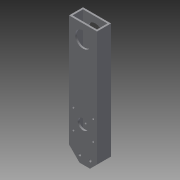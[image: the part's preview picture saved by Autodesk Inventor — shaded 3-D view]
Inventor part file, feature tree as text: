
AUTODESK INVENTOR PART (.ipt)
format: ipt  version: 2013 (Build 170138000, 138)  size: 178,176 bytes
history: native  units: in
note: dims shown in document units (in); Inventor stores cm internally (conversion verified against a paired STEP export)
features: extrude x7, sketch x7
ambient origin geometry x8: Origin, YZ Plane, XZ Plane, XY Plane, X Axis, Y Axis, Z Axis, Center Point
bodies: Solid1 (feature_tree)
feature tree (14):
  extrude  "Extrusion1"  Depth=1.0in
  extrude  "Extrusion2"  Depth=0.75in
  extrude  "Extrusion3"  Depth=1.0in
  extrude  "Extrusion4"  Depth=7.0in
  extrude  "Extrusion5"  Depth=0.25in
  extrude  "Extrusion6"  Depth=0.5in
  extrude  "Extrusion7"  TaperAngle=0.0deg  [1 undecoded]
  sketch  "Sketch1"  dims[d0=2.0in d1=1.0in]
  sketch  "Sketch2"  dims[d2=1.75in d3=0.75in]
  sketch  "Sketch3"  dims[d4=9.0in d5=0.0in d6=1.0in]
  sketch  "Sketch4"  dims[d7=0.5in d8=7.0in]
  sketch  "Sketch5"  dims[d9=90.0deg d10=0.25in]
  sketch  "Sketch6"  dims[d11=90.0deg d12=0.5in]
  sketch  "Sketch7"  dims[d13=0.75in d14=0.0in d15=0.2in d16=0.2in d17=9.0in d18=0.0in d19=0.25in d20=0.0in d21=25.0in d22=0.0in d23=25.0in d24=0.0in d25=2.5in d26=90.0deg d27=0.75in d28=1.0in d29=45.0deg d30=2.0in d31=0.16in d32=0.16in d33=0.16in d34=0.16in d35=25.0in d36=0.0in d37=1.125in d38=25.0in d39=0.0in]
note: 1 required parameter value undecoded (feature->parameter linkage not recoverable at this tier; creation-order binding heuristic only, values carry confidence <= 0.55)
